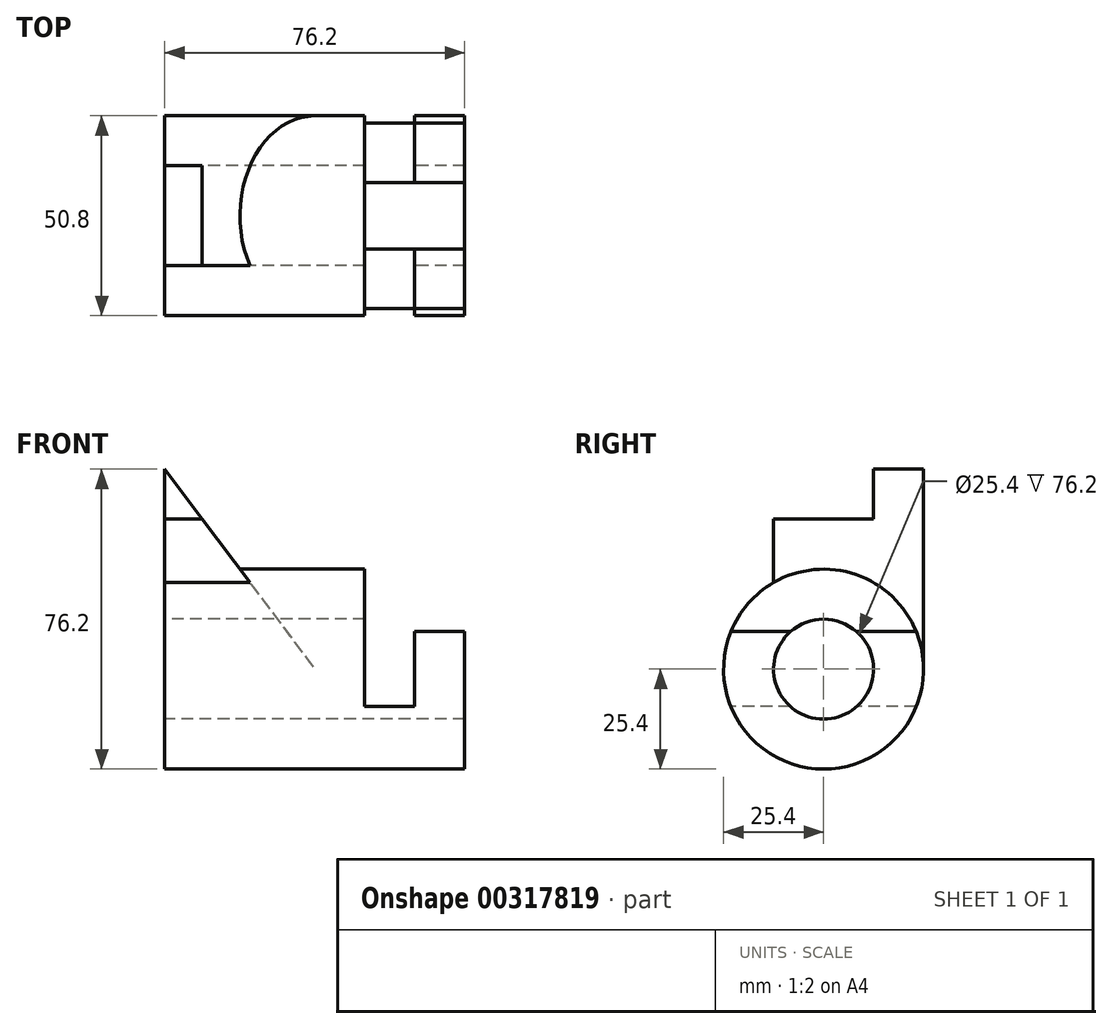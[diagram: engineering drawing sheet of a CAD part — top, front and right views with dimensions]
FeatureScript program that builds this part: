
annotation { "Feature Type Name" : "Feature", "Feature Type Description" : "" }
export const myFeature = defineFeature(function(context is Context, id is Id, definition is map)
    precondition{}
    {
        {
            var Q0;
            Q0=qCreatedBy(makeId("Right.planeOp"),FACE);
            var sketch = newSketch(context, id + "F0", { "sketchPlane" : qUnion([Q0])});
            skCircle(sketch, "E0", {"center": v(0, 0) * mm, "radius": 25.4 * mm});
            skCircle(sketch, "E1", {"center": v(0, 0) * mm, "radius": 12.7 * mm});
            skSolve(sketch);
        }
        {
            var Q0;
            Q0 = qSketchRegion(id + "F0", true);
            extrude(context, id + "F1", {"entities" : qUnion([Q0]), "depth" : 76.2 * mm});
        }
        {
            var Q0;
            Q0=qCreatedBy(makeId("Front.planeOp"),FACE);
            var sketch = newSketch(context, id + "F2", { "sketchPlane" : qUnion([Q0])});
            skLineSegment(sketch, "E2", {"start": v(50.8, -9.52) * mm, "end": v(50.8, 25.4) * mm});
            skLineSegment(sketch, "E3", {"start": v(50.8, 25.4) * mm, "end": v(50.8, -9.52) * mm});
            skLineSegment(sketch, "E4", {"start": v(50.8, -9.53) * mm, "end": v(63.5, -9.53) * mm});
            skLineSegment(sketch, "E5", {"start": v(63.5, 9.53) * mm, "end": v(63.5, -9.53) * mm});
            skLineSegment(sketch, "E6", {"start": v(63.5, 9.53) * mm, "end": v(76.2, 9.53) * mm});
            skLineSegment(sketch, "E7", {"start": v(76.2, 9.53) * mm, "end": v(76.2, 25.4) * mm});
            skLineSegment(sketch, "E8", {"start": v(50.8, 25.4) * mm, "end": v(76.2, 25.4) * mm});
            skSolve(sketch);
        }
        {
            var Q0;
            Q0 = qSketchRegion(id + "F2", true);
            extrude(context, id + "F3", {"entities" : qUnion([Q0]), "operationType" : NewBodyOperationType.REMOVE, "endBound" : BoundingType.THROUGH_ALL, "oppositeDirection" : true, "depth" : 25.4 * mm, "hasSecondDirection" : true, "secondDirectionBound" : SecondDirectionBoundingType.THROUGH_ALL, "secondDirectionOppositeDirection" : false, "secondDirectionDepth" : 25.4 * mm});
        }
        {
            var Q0;
            Q0=qCreatedBy(makeId("Front.planeOp"),FACE);
            var sketch = newSketch(context, id + "F4", { "sketchPlane" : qUnion([Q0])});
            skLineSegment(sketch, "E9", {"start": v(0, 0) * mm, "end": v(0, 50.8) * mm});
            skLineSegment(sketch, "E10", {"start": v(0, 50.8) * mm, "end": v(38.1, 0) * mm});
            skLineSegment(sketch, "E11", {"start": v(0, 0) * mm, "end": v(38.1, 0) * mm});
            skSolve(sketch);
        }
        {
            var Q0;
            Q0 = qSketchRegion(id + "F4", true);
            extrude(context, id + "F5", {"entities" : qUnion([Q0]), "operationType" : NewBodyOperationType.ADD, "oppositeDirection" : true, "depth" : 25.4 * mm, "hasSecondDirection" : true, "secondDirectionOppositeDirection" : false, "secondDirectionDepth" : 12.7 * mm});
        }
        {
            var Q0;
            Q0=makeQuery(id+"F5.boolean.opBoolean","MERGE",FACE,{"derivedFrom":[makeQuery(id+"F1.opExtrude","CAP_FACE",FACE,{"disambiguationData":[OSD([sQuery(id+"F0.wireOp",EDGE,"E0"),sQuery(id+"F0.wireOp",EDGE,"E1")])],"isStart":true}),makeQuery(id+"F5.opExtrude","SWEPT_FACE",FACE,{"disambiguationData":[OSD([sQuery(id+"F4.wireOp",EDGE,"E9")])]})]});
            var sketch = newSketch(context, id + "F6", { "sketchPlane" : qUnion([Q0])});
            skCircle(sketch, "E12", {"center": v(0, 0) * mm, "radius": 12.7 * mm});
            skSolve(sketch);
        }
        {
            var Q0;
            Q0 = qSketchRegion(id + "F6", true);
            extrude(context, id + "F7", {"entities" : qUnion([Q0]), "operationType" : NewBodyOperationType.REMOVE, "endBound" : BoundingType.THROUGH_ALL, "oppositeDirection" : true, "depth" : 25.4 * mm});
        }
        {
            var Q0;
            Q0=makeQuery(id+"F5.opExtrude","CAP_FACE",FACE,{"disambiguationData":[OSD([sQuery(id+"F4.wireOp",EDGE,"E9"),sQuery(id+"F4.wireOp",EDGE,"E10"),sQuery(id+"F4.wireOp",EDGE,"E11")])],"isStart":true});
            var sketch = newSketch(context, id + "F8", { "sketchPlane" : qUnion([Q0])});
            skLineSegment(sketch, "E13", {"start": v(0, 50.8) * mm, "end": v(0, 38.1) * mm});
            skLineSegment(sketch, "E14", {"start": v(0, 50.8) * mm, "end": v(9.53, 38.1) * mm});
            skLineSegment(sketch, "E15", {"start": v(0, 38.1) * mm, "end": v(9.53, 38.1) * mm});
            skSolve(sketch);
        }
        {
            var Q0;
            Q0 = qSketchRegion(id + "F8", true);
            extrude(context, id + "F9", {"entities" : qUnion([Q0]), "operationType" : NewBodyOperationType.REMOVE, "oppositeDirection" : true, "depth" : 25.4 * mm});
        }
    });
